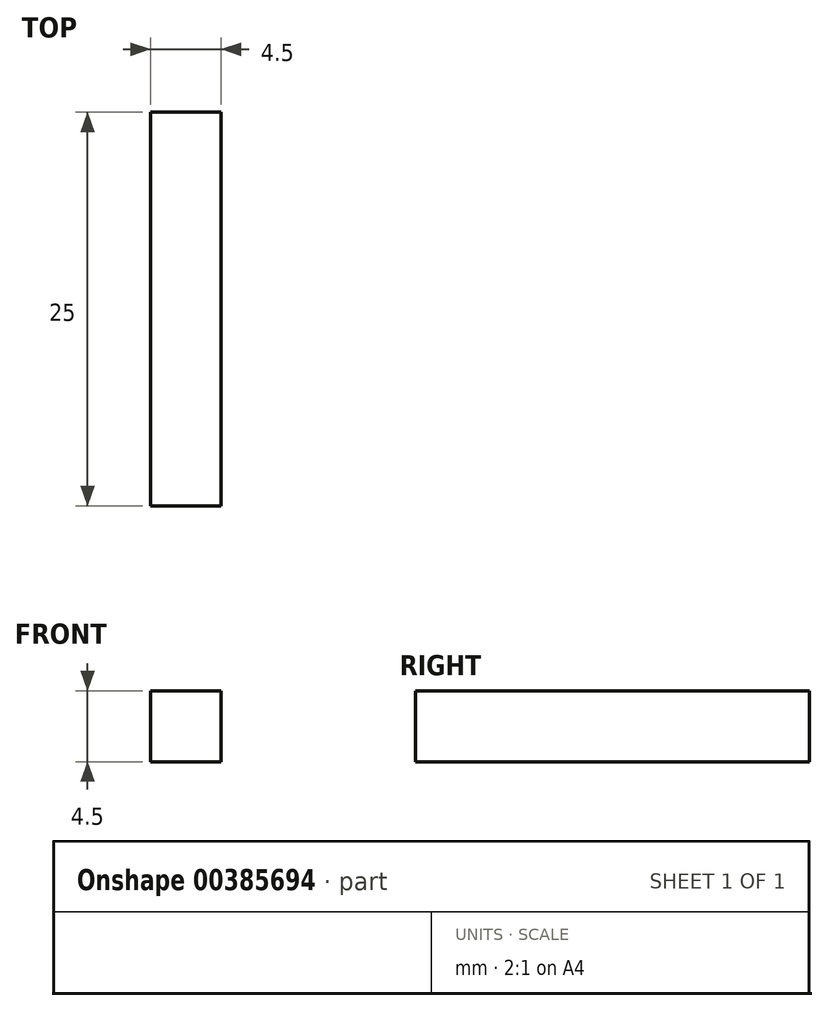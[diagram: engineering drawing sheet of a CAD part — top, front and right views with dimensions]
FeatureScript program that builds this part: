
annotation { "Feature Type Name" : "Feature", "Feature Type Description" : "" }
export const myFeature = defineFeature(function(context is Context, id is Id, definition is map)
    precondition{}
    {
        {
            var Q0;
            Q0=qCreatedBy(makeId("Front.planeOp"),FACE);
            var sketch = newSketch(context, id + "F0", { "sketchPlane" : qUnion([Q0])});
            skLineSegment(sketch, "E0.bottom", {"start": v(-2, 1.27) * mm, "end": v(2.5, 1.27) * mm});
            skLineSegment(sketch, "E0.top", {"start": v(-2, -3.23) * mm, "end": v(2.5, -3.23) * mm});
            skLineSegment(sketch, "E0.left", {"start": v(-2, 1.27) * mm, "end": v(-2, -3.23) * mm});
            skLineSegment(sketch, "E0.right", {"start": v(2.5, 1.27) * mm, "end": v(2.5, -3.23) * mm});
            skSolve(sketch);
        }
        {
            var Q0;
            Q0 = qSketchRegion(id + "F0", true);
            extrude(context, id + "F1", {"entities" : qUnion([Q0]), "depth" : 25 * mm});
        }
    });
